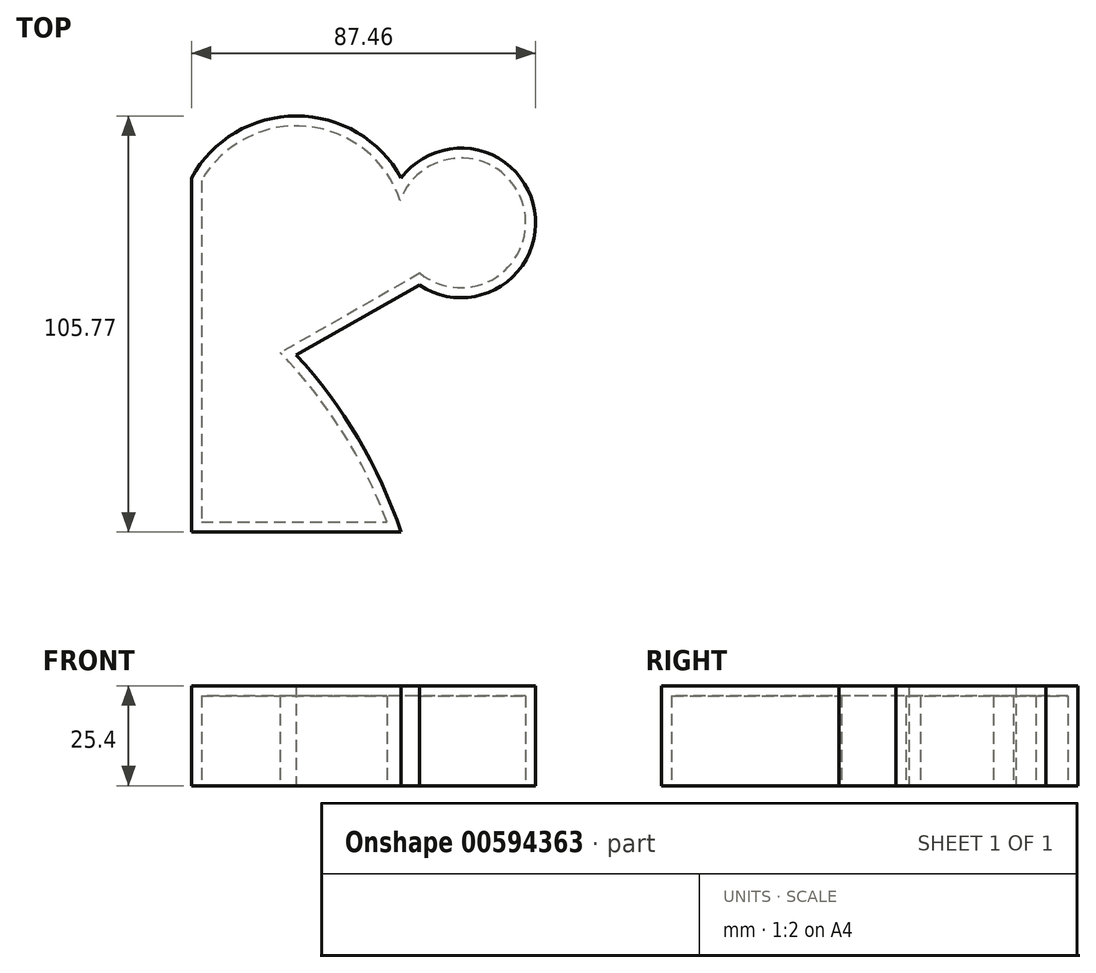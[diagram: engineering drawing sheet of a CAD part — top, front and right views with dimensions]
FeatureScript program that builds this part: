
annotation { "Feature Type Name" : "Feature", "Feature Type Description" : "" }
export const myFeature = defineFeature(function(context is Context, id is Id, definition is map)
    precondition{}
    {
        {
            var Q0;
            Q0=qCreatedBy(makeId("Top.planeOp"),FACE);
            var sketch = newSketch(context, id + "F0", { "sketchPlane" : qUnion([Q0])});
            skLineSegment(sketch, "E0.top", {"start": v(-26.64, -45) * mm, "end": v(26.64, -45) * mm});
            skLineSegment(sketch, "E0.left", {"start": v(-26.64, 45) * mm, "end": v(-26.64, -45) * mm});
            skPoint(sketch, "E0.middle", {"position": v(0, 0) * mm});
            skArc(sketch, "E1", {"start": v(26.64, 45) * mm, "mid": v(0, 60.77) * mm, "end": v(-26.64, 45) * mm});
            skPoint(sketch, "E2.orphan", {"position": v(26.64, 45) * mm});
            skArc(sketch, "E3", {"start": v(31.26, 17.77) * mm, "mid": v(60.55, 36.76) * mm, "end": v(26.64, 45) * mm});
            skLineSegment(sketch, "E4", {"start": v(31.26, 17.77) * mm, "end": v(0, 0) * mm});
            skArc(sketch, "E5", {"start": v(26.64, -45) * mm, "mid": v(15.68, -21.1) * mm, "end": v(0, 0) * mm});
            skSolve(sketch);
        }
        {
            var Q0;
            Q0 = qSketchRegion(id + "F0", true);
            extrude(context, id + "F1", {"entities" : qUnion([Q0]), "depth" : 25.4 * mm, "offsetDistance" : 25.4 * mm});
        }
        {
            var Q0;
            Q0=makeQuery(id+"F1.opExtrude","CAP_FACE",FACE,{"disambiguationData":[OSD([sQuery(id+"F0.wireOp",EDGE,"E0.top"),sQuery(id+"F0.wireOp",EDGE,"E0.left"),sQuery(id+"F0.wireOp",EDGE,"E1"),sQuery(id+"F0.wireOp",EDGE,"E3"),sQuery(id+"F0.wireOp",EDGE,"E4"),sQuery(id+"F0.wireOp",EDGE,"E5")])],"isStart":true});
            shell(context, id + "F2", {"entities" : qUnion([Q0]), "thickness" : 2.54 * mm});
        }
    });
